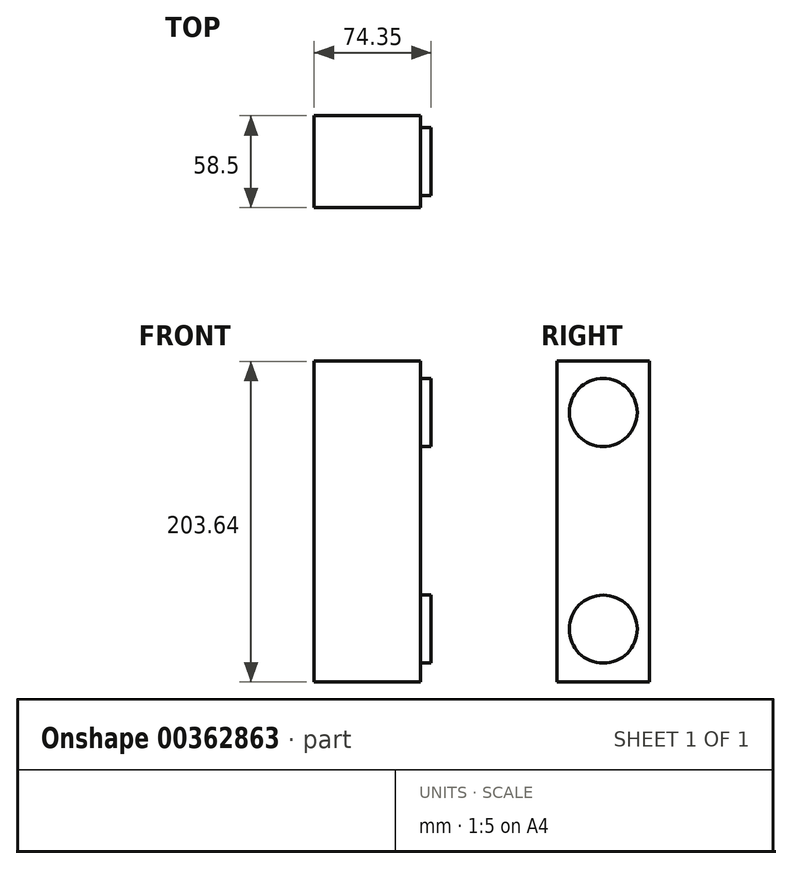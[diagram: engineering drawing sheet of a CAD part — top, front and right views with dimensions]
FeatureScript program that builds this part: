
annotation { "Feature Type Name" : "Feature", "Feature Type Description" : "" }
export const myFeature = defineFeature(function(context is Context, id is Id, definition is map)
    precondition{}
    {
        {
            var Q0;
            Q0=qCreatedBy(makeId("Top.planeOp"),FACE);
            var sketch = newSketch(context, id + "F0", { "sketchPlane" : qUnion([Q0])});
            skLineSegment(sketch, "E0.bottom", {"start": v(33.82, 29.25) * mm, "end": v(-33.82, 29.25) * mm});
            skLineSegment(sketch, "E0.top", {"start": v(33.82, -29.25) * mm, "end": v(-33.82, -29.25) * mm});
            skLineSegment(sketch, "E0.left", {"start": v(33.82, 29.25) * mm, "end": v(33.82, -29.25) * mm});
            skLineSegment(sketch, "E0.right", {"start": v(-33.82, 29.25) * mm, "end": v(-33.82, -29.25) * mm});
            skPoint(sketch, "E0.middle", {"position": v(0, 0) * mm});
            skSolve(sketch);
        }
        {
            var Q0;
            Q0=makeQuery(id+"F0.imprint","IMPRINT",FACE,{"disambiguationData":[TD([[makeQuery(id+"F0.imprint","IMPRINT",EDGE,{"derivedFrom":sQuery(id+"F0.wireOp",EDGE,"E0.bottom")}),1.0]])]});
            extrude(context, id + "F1", {"entities" : qUnion([Q0]), "depth" : 101.34 * mm, "hasSecondDirection" : true, "secondDirectionOppositeDirection" : true, "secondDirectionDepth" : 102.3 * mm});
        }
        {
            var Q0;
            Q0=makeQuery(id+"F1.opExtrude","SWEPT_FACE",FACE,{"disambiguationData":[OSD([sQuery(id+"F0.wireOp",EDGE,"E0.left")])]});
            var sketch = newSketch(context, id + "F2", { "sketchPlane" : qUnion([Q0])});
            skCircle(sketch, "E1", {"center": v(0, 68.83) * mm, "radius": 21.6 * mm});
            skLineSegment(sketch, "E2", {"start": v(21.6, 101.34) * mm, "end": v(21.6, -102.3) * mm, "construction": true});
            skLineSegment(sketch, "E3", {"start": v(-29.25, 0) * mm, "end": v(29.25, 0) * mm, "construction": true});
            skCircle(sketch, "E4.MirrorC", {"center": v(0, -68.83) * mm, "radius": 21.6 * mm});
            skSolve(sketch);
        }
        {
            var Q0;
            Q0 = qSketchRegion(id + "F2", true);
            extrude(context, id + "F3", {"entities" : qUnion([Q0]), "operationType" : NewBodyOperationType.ADD, "depth" : 6.72 * mm});
        }
    });
